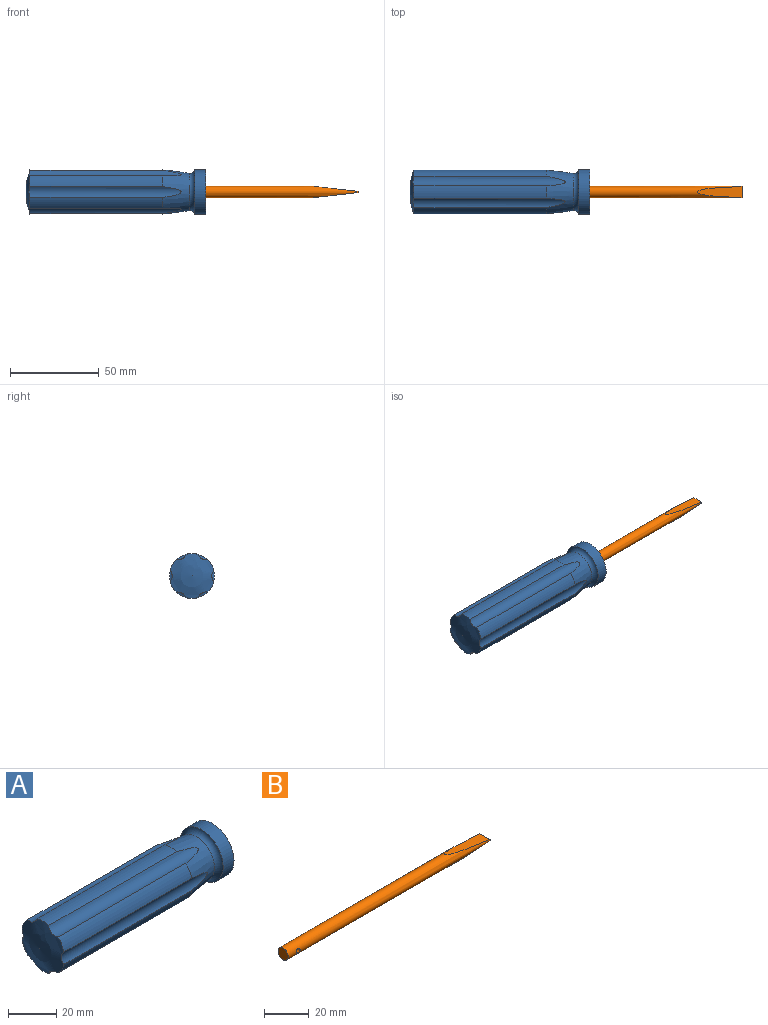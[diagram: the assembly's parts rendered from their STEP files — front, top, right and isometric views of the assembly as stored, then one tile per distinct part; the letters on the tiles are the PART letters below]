
ASSEMBLY  parts=2 mates=1
PART A: 19 faces, bbox 101.6x28.1x28.1 mm
  f0: cylinder r=12.7mm len=75.04mm, axis (1,0,0), area 526.2mm2, adj f6,f10,f11,f16
  f1: cylinder r=12.7mm len=75.04mm, axis (1,0,0), area 526.2mm2, adj f6,f10,f15,f16
  f2: cylinder r=12.7mm len=75.04mm, axis (1,0,0), area 526.2mm2, adj f6,f10,f14,f15
  f3: cylinder r=12.7mm len=75.04mm, axis (1,0,0), area 526.2mm2, adj f6,f10,f13,f14
  f4: cylinder r=12.7mm len=75.04mm, axis (1,0,0), area 526.2mm2, adj f6,f10,f12,f13
  f5: cylinder r=12.7mm len=75.04mm, axis (1,0,0), area 526.2mm2, adj f6,f10,f11,f12
  f6: sphere r=38.1mm, area 480.8mm2, adj f0,f1,f2,f3,f4,f5,f11,f12
  f7: plane 25.4x25.4mm, normal (1,0,0), area 475mm2, adj f8,f17
  f8: cylinder r=12.7mm len=25.4mm, axis (1,0,0), area 507.9mm2, adj f7,f9
  f9: torus R=12.98mm, axis (1,0,0), area 286.9mm2, adj f8,f10
  f10: cone r=12.7mm half-angle=8.4deg, axis (-1,0,0), area 847.3mm2, adj f0,f1,f2,f3,f4,f5,f9,f11
  f11: cylinder r=4.83mm len=85.85mm, axis (1,0,0), area 555.2mm2, adj f0,f5,f6,f10
  f12: cylinder r=4.83mm len=85.85mm, axis (1,0,0), area 555.2mm2, adj f4,f5,f6,f10
  f13: cylinder r=4.83mm len=85.85mm, axis (1,0,0), area 555.2mm2, adj f3,f4,f6,f10
  f14: cylinder r=4.83mm len=85.85mm, axis (1,0,0), area 555.2mm2, adj f2,f3,f6,f10
  f15: cylinder r=4.83mm len=85.85mm, axis (1,0,0), area 555.2mm2, adj f1,f2,f6,f10
  f16: cylinder r=4.83mm len=85.85mm, axis (1,0,0), area 555.2mm2, adj f0,f1,f6,f10
  f17: cylinder r=3.17mm len=41.15mm, axis (1,0,0), area 820.9mm2, adj f7,f18
  f18: plane 6.35x6.35mm, normal (1,0,0), area 31.7mm2, adj f17
PART B: 6 faces, bbox 127x6.4x6.4 mm
  f0: cylinder r=3.17mm len=127mm, axis (1,0,0), area 2224.1mm2, adj f1,f2,f3,f4,f5
  f1: plane 6.35x0.76mm, normal (1,0,0), area 4.8mm2, adj f0,f3,f4
  f2: plane 6.35x6.35mm, normal (-1,0,0), area 31.7mm2, adj f0
  f3: plane 25.4x6.3mm, normal (0.11,0,0.99), area 122.7mm2, adj f0,f1
  f4: plane 25.4x6.3mm, normal (0.11,0,-0.99), area 122.7mm2, adj f0,f1
  f5: cylinder r=1.21mm len=6.35mm, axis (0,-1,0), area 46.3mm2, adj f0
PLACE A t=(-21.09,0.45,0.2)mm
PLACE B t=(64.76,0.45,0.2)mm
MATE fastened A.f17 <-> B.f0  axis (1,0,0) through (-62.24,0.45,0.2)mm
